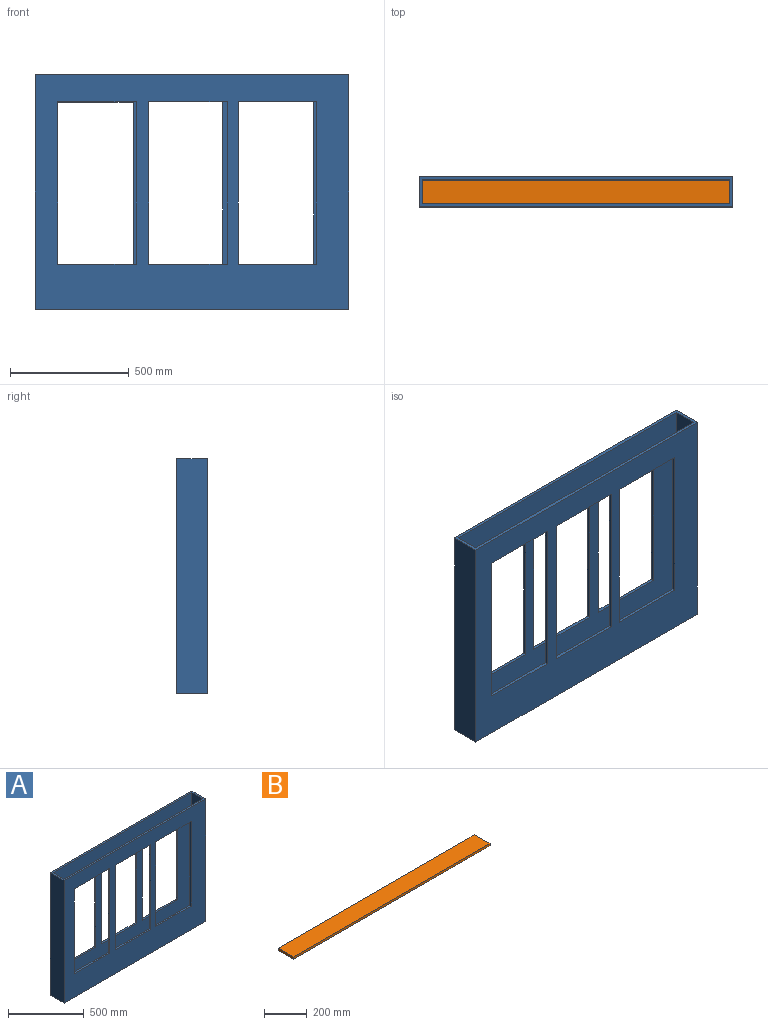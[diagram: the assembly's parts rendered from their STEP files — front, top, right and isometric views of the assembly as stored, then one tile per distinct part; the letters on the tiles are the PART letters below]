
ASSEMBLY  parts=2 mates=1
PART A: 34 faces, bbox 1320.8x127x990.6 mm
  f0: plane 1295.4x990.6mm, normal (0,1,0), area 602552.7mm2, adj f3,f7,f8,f9,f10,f11,f12,f13
  f1: plane 1320.8x990.6mm, normal (0,-1,0), area 627714mm2, adj f4,f5,f8,f9,f10,f11,f12,f13
  f2: plane 1295.4x990.6mm, normal (0,-1,0), area 603869.8mm2, adj f3,f7,f8,f9,f22,f23,f24,f25
  f3: plane 990.6x101.6mm, normal (1,0,0), area 100645mm2, adj f0,f2,f8,f9
  f4: plane 990.6x127mm, normal (1,0,0), area 125806.2mm2, adj f1,f6,f8,f9
  f5: plane 990.6x127mm, normal (-1,0,0), area 125806.2mm2, adj f1,f6,f8,f9
  f6: plane 1320.8x990.6mm, normal (0,1,0), area 629031mm2, adj f4,f5,f8,f9,f22,f23,f24,f25
  f7: plane 990.6x101.6mm, normal (-1,0,0), area 100645mm2, adj f0,f2,f8,f9
  f8: plane 1320.8x127mm, normal (0,0,-1), area 36129mm2, adj f0,f1,f2,f3,f4,f5,f6,f7
  f9: plane 1320.8x127mm, normal (0,0,1), area 36129mm2, adj f0,f1,f2,f3,f4,f5,f6,f7
  f10: plane 331.54x12.7mm, normal (0,0,-1), area 4210.5mm2, adj f0,f1,f11,f13
  f11: plane 685.2x12.7mm, normal (1,0,0), area 8702.1mm2, adj f0,f1,f10,f12
  f12: plane 331.54x12.7mm, normal (0,0,1), area 4210.5mm2, adj f0,f1,f11,f13
  f13: plane 685.2x12.7mm, normal (-1,0,0), area 8702.1mm2, adj f0,f1,f10,f12
  f14: plane 330.31x12.7mm, normal (0,0,-1), area 4194.9mm2, adj f0,f1,f15,f17
  f15: plane 685.2x12.7mm, normal (1,0,0), area 8702.1mm2, adj f0,f1,f14,f16
  f16: plane 330.31x12.7mm, normal (0,0,1), area 4194.9mm2, adj f0,f1,f15,f17
  f17: plane 685.2x12.7mm, normal (-1,0,0), area 8702.1mm2, adj f0,f1,f14,f16
  f18: plane 331.54x12.7mm, normal (0,0,-1), area 4210.5mm2, adj f0,f1,f19,f21
  f19: plane 685.2x12.7mm, normal (1,0,0), area 8702.1mm2, adj f0,f1,f18,f20
  f20: plane 331.54x12.7mm, normal (0,0,1), area 4210.5mm2, adj f0,f1,f19,f21
  f21: plane 685.2x12.7mm, normal (-1,0,0), area 8702.1mm2, adj f0,f1,f18,f20
  f22: plane 685.8x12.7mm, normal (1,0,0), area 8709.7mm2, adj f2,f6,f23,f25
  f23: plane 330.2x12.7mm, normal (0,0,-1), area 4193.5mm2, adj f2,f6,f22,f24
  f24: plane 685.8x12.7mm, normal (-1,0,0), area 8709.7mm2, adj f2,f6,f23,f25
  f25: plane 330.2x12.7mm, normal (0,0,1), area 4193.5mm2, adj f2,f6,f22,f24
  f26: plane 685.8x12.7mm, normal (1,0,0), area 8709.7mm2, adj f2,f6,f27,f29
  f27: plane 330.2x12.7mm, normal (0,0,-1), area 4193.5mm2, adj f2,f6,f26,f28
  f28: plane 685.8x12.7mm, normal (-1,0,0), area 8709.7mm2, adj f2,f6,f27,f29
  f29: plane 330.2x12.7mm, normal (0,0,1), area 4193.5mm2, adj f2,f6,f26,f28
  f30: plane 685.8x12.7mm, normal (1,0,0), area 8709.7mm2, adj f2,f6,f31,f33
  f31: plane 330.2x12.7mm, normal (0,0,-1), area 4193.5mm2, adj f2,f6,f30,f32
  f32: plane 685.8x12.7mm, normal (-1,0,0), area 8709.7mm2, adj f2,f6,f31,f33
  f33: plane 330.2x12.7mm, normal (0,0,1), area 4193.5mm2, adj f2,f6,f30,f32
PART B: 6 faces, bbox 1295.4x101.6x12.7 mm
  f0: plane 101.6x12.7mm, normal (-1,0,0), area 1290.3mm2, adj f1,f3,f4,f5
  f1: plane 1295.4x12.7mm, normal (0,1,0), area 16451.6mm2, adj f0,f2,f4,f5
  f2: plane 101.6x12.7mm, normal (1,0,0), area 1290.3mm2, adj f1,f3,f4,f5
  f3: plane 1295.4x12.7mm, normal (0,-1,0), area 16451.6mm2, adj f0,f2,f4,f5
  f4: plane 1295.4x101.6mm, normal (0,0,1), area 131612.6mm2, adj f0,f1,f2,f3
  f5: plane 1295.4x101.6mm, normal (0,0,-1), area 131612.6mm2, adj f0,f1,f2,f3
PLACE A t=(-230.31,196.02,-362.13)mm
PLACE B t=(-908.46,498.34,-362.13)mm
MATE fastened B.f5 <-> A.f8  axis (0,0,1) through (-852.04,337.14,133.17)mm
